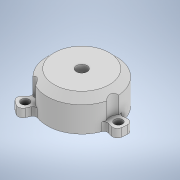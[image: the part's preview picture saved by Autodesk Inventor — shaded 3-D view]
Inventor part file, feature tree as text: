
AUTODESK INVENTOR PART (.ipt)
format: ipt  version: 2022 (Build 260153000, 153)  size: 387,072 bytes
history: native  units: in
note: dims shown in document units (in); Inventor stores cm internally (conversion verified against a paired STEP export)
features: extrude x10, sketch x10, projected_geometry x10, fillet x3, thicken_offset x3, reference x3, other x3, chamfer x1
ambient origin geometry x8: Origin, YZ Plane, XZ Plane, XY Plane, X Axis, Y Axis, Z Axis, Center Point
bodies: Solid1 (feature_tree)
feature tree (43):
  extrude  "Extrusion1"  Depth=1.0in
  extrude  "Extrusion3"  Depth=0.875in
  extrude  "Extrusion4"  Depth=0.0591in
  extrude  "Extrusion5"  Depth=0.05in
  fillet  "Fillet1"  Radius=0.15in
  extrude  "Extrusion6"  Depth=0.15in
  fillet  "Fillet2"  Radius=0.0787in
  chamfer  "Chamfer2"  Distance=7.874in Angle=360.0deg
  extrude  "Extrusion7"  Depth=0.275in
  extrude  "Extrusion8"  Depth=0.125in
  fillet  "Fillet3"  Radius=0.05in
  thicken_offset  "Thicken3"
  thicken_offset  "Thicken4"
  thicken_offset  "Thicken5"
  extrude  "Extrusion9"  TaperAngle=135.0deg  [1 undecoded]
  extrude  "Extrusion10"  Depth=0.125in
  extrude  "Extrusion11"  Depth=0.125in TaperAngle=0.0deg
  sketch  "Sketch1"  dims[d0=0.1575in d1=1.0in]
  sketch  "Sketch3"  dims[d2=0.1181in d3=0.0in d14=0.875in]
  sketch  "Sketch4"  dims[d15=0.3487in d16=0.0in d17=0.0591in]
  projected_geometry  "Projected Loop2"
  projected_geometry  "Projected Loop3"
  sketch  "Sketch5"  dims[d18=0.3in d19=0.05in d20=0.15in]
  projected_geometry  "Projected Loop4"
  sketch  "Sketch8"  dims[d21=0.05in d22=0.15in d23=0.0787in d24=0.0in]
  reference  "Reference5"
  reference  "Reference6"
  reference  "Reference7"
  sketch  "Sketch9"  dims[d28=0.075in]
  projected_geometry  "Projected Loop5"
  projected_geometry  "Projected Loop6"
  sketch  "Sketch10"  dims[d29=45.0deg]
  sketch  "Sketch11"  dims[d30=135.0deg d31=7.874in d33=360.0deg]
  projected_geometry  "Projected Loop7"
  sketch  "Sketch12"  dims[d35=0.0787in d36=0.0in d37=0.275in]
  projected_geometry  "Projected Loop8"
  sketch  "Sketch13"  dims[d38=0.05in d39=0.15in d40=0.05in d41=135.0deg d42=0.05in d43=0.2in d44=0.0in d45=0.05in d46=0.1in d47=0.125in d48=45.0deg d49=0.2362in d50=0.315in d51=0.25in d52=0.0in d53=0.25in d54=0.25in d55=0.25in d56=0.1181in d57=0.0in d58=0.07in d59=0.025in d60=0.025in d61=0.025in d62=0.025in d63=0.025in d64=0.025in d65=1.0in d66=0.0in d67=0.12in d68=0.0in d69=0.25in d70=0.25in d71=0.25in d72=0.12in d73=0.0in]
  projected_geometry  "Projected Loop9"
  projected_geometry  "Projected Loop10"
  projected_geometry  "Projected Loop11"
  parser-record x1  (decoder bookkeeping rows leaked as tree rows — omitted from the tree; the rows remain in map.json)
  other  "Assembly1.iam"
  other  "CubeKnob:1"
note: 1 required parameter value undecoded (feature->parameter linkage not recoverable at this tier; creation-order binding heuristic only, values carry confidence <= 0.55)
note: 1 file-system path scrubbed to <path> (originals preserved in map.json)
